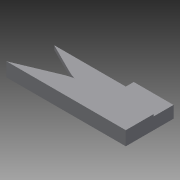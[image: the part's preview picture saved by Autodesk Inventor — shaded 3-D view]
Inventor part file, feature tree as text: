
AUTODESK INVENTOR PART (.ipt)
format: ipt  version: 2015 (Build 190159000, 159)  size: 99,840 bytes
history: native  units: in
note: dims shown in document units (in); Inventor stores cm internally (conversion verified against a paired STEP export)
features: extrude x3, sketch x1, fillet x1
ambient origin geometry x8: Origin, YZ Plane, XZ Plane, XY Plane, X Axis, Y Axis, Z Axis, Center Point
bodies: Body1 (feature_tree)
feature tree (5):
  sketch  "Sketch1"  dims[d13=0.0787in d15=0.3937in d38=0.0394in d39=0.0in d40=0.1181in d41=0.0in d42=0.1378in d43=0.0in d44=0.3937in]
  extrude  "Extrusion6"  Depth=0.3937in
  extrude  "Extrusion7"  Depth=0.0394in TaperAngle=0.0deg
  extrude  "Extrusion8"  Depth=0.1181in TaperAngle=0.0deg
  fillet  "Fillet4"  Radius=0.1378in
